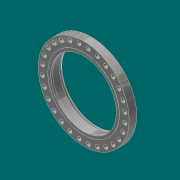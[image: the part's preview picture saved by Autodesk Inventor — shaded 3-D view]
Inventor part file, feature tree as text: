
AUTODESK INVENTOR PART (.ipt)
format: ipt  version: 2017.3 (Build 213257000, 257)  size: 377,344 bytes
history: native  units: in
note: dims shown in document units (in); Inventor stores cm internally (conversion verified against a paired STEP export)
features: sketch x6, extrude x4, chamfer x4, fillet x2, hole x1, pattern_circular x1, revolve x1, projected_geometry x1
ambient origin geometry x8: Origin, YZ Plane, XZ Plane, XY Plane, X Axis, Y Axis, Z Axis, Center Point
bodies: Solid1 (feature_tree)
feature tree (20):
  extrude  "Extrusion1"  Depth=31.0in
  extrude  "Extrusion2"  Depth=3.625in
  extrude  "Extrusion3"  Depth=0.0625in
  extrude  "Extrusion9"  Depth=19.625in
  hole  "Hole1"  [1 undecoded]
  chamfer  "Chamfer3"  Distance=0.0625in
  pattern_circular  "Circular Pattern1"  [2 undecoded]
  chamfer  "Chamfer2"  Distance=0.0312in Angle=45.0deg
  fillet  "Fillet2"  Radius=0.0625in
  chamfer  "Chamfer4"  Distance=34.0in
  revolve  "Revolution3"  [1 undecoded]
  fillet  "Fillet7"  Radius=0.125in
  chamfer  "Chamfer8"  Distance=0.25in
  sketch  "Sketch1"  dims[d0=43.0in d1=31.0in]
  sketch  "Sketch2"  dims[d2=3.625in d3=0.0in d4=33.75in]
  sketch  "Sketch3"  dims[d5=0.0625in d6=0.0in d7=34.75in]
  sketch  "Sketch4"  dims[d8=2.4375in d9=0.0in d13=19.625in]
  sketch  "Sketch12"  dims[d14=0.0442in]
  sketch  "Sketch15"  dims[d15=1.875in d16=0.75in d17=0.375in d18=0.25in d19=0.5635in d20=1.0in d21=0.8108in d22=11.0236in d23=360.0deg d25=0.0625in d26=0.125in d27=0.0687in d29=0.4375in d30=0.0312in d31=0.125in d32=45.0deg d33=0.0625in d34=0.125in d35=45.0deg d98=34.0in d99=0.4375in d100=0.125in d101=0.25in d102=0.2577in d103=0.5in d104=0.875in d105=0.2893in d106=31.375in d108=90.0deg d109=0.0312in d110=0.0312in d111=0.125in d112=45.0deg d120=1.0in d129=1.0in d130=0.0in d134=0.0625in d135=0.1718in]
  projected_geometry  "Projected Loop1"
note: 4 required parameter values undecoded (feature->parameter linkage not recoverable at this tier; creation-order binding heuristic only, values carry confidence <= 0.55)